# Revit family: Sink-Kitchen-KOHLER-Cairn-K-28001
name_source: partatom
category: Plumbing Fixtures
revit_build: Autodesk Revit 2015 (Build: 20140606_1530(x64)
units: mm (PartAtom-declared; Revit-internal decimal feet)

## types (6) — shared parameters
ADA Compliant = No
Assembly Code = D2010400
CW Connection = No
Cold Water Inlet = Cold Water Inlet
Date Modified = 01/30/2019
Default Elevation = 36"
Description = 24-1/2 Inch x 18-5/16 Inch x 9-1/2 Inch Neoroc under-mount single-bowl kitchen sink with sink rack
Drain Included = No
HW Connection = No
Height = 10 3/16"
Hot Water Inlet = Hot Water Inlet
Length = 24 1/2"
Manufacturer = KOHLER Co.
MasterFormat 1995 = 15410
MasterFormat 2004 = 22.41.16
Material = Neoroc
Product Documentation Link = https://www.us.kohler.com
Product Name = Cairn
Product Page URL = http://www.us.kohler.com
URL = https://www.us.kohler.com
Vent Connection = No
Waste Connection = Yes
Waste Water Outlet = Waste Water Outlet
WaterSense Certified = No
Width = 18 5/16"

## per-type parameters (varying)
| type | Finish | Model | Type |
| CM1- Matte Black | Kohler-Neoroc-CM1-Matte_Black | K-28001-CM1 | 1 |
| CM6- Matte White | Kohler-Neoroc-CM6-Matte_White | K-28001-CM6 | 5 |
| CM3- Matte Taupe | Kohler-Neoroc-CM3-Matte_Taupe | K-28001-CM3 | 3 |
| CM4- Matte Grey | Kohler-Neoroc-CM4-Matte_Grey | K-28001-CM4 | 4 |
| CM2- Matte Brown | Kohler-Neoroc-CM2-Matte_Brown | K-28001-CM2 | 2 |
| CM7- Matte Graphite | Kohler-Neoroc-CM7-Matte_Graphite | K-28001-CM7 | 6 |

## geometry (parser evidence)
native form markers: Sweep x6
no freeform markers — native parametric forms only
